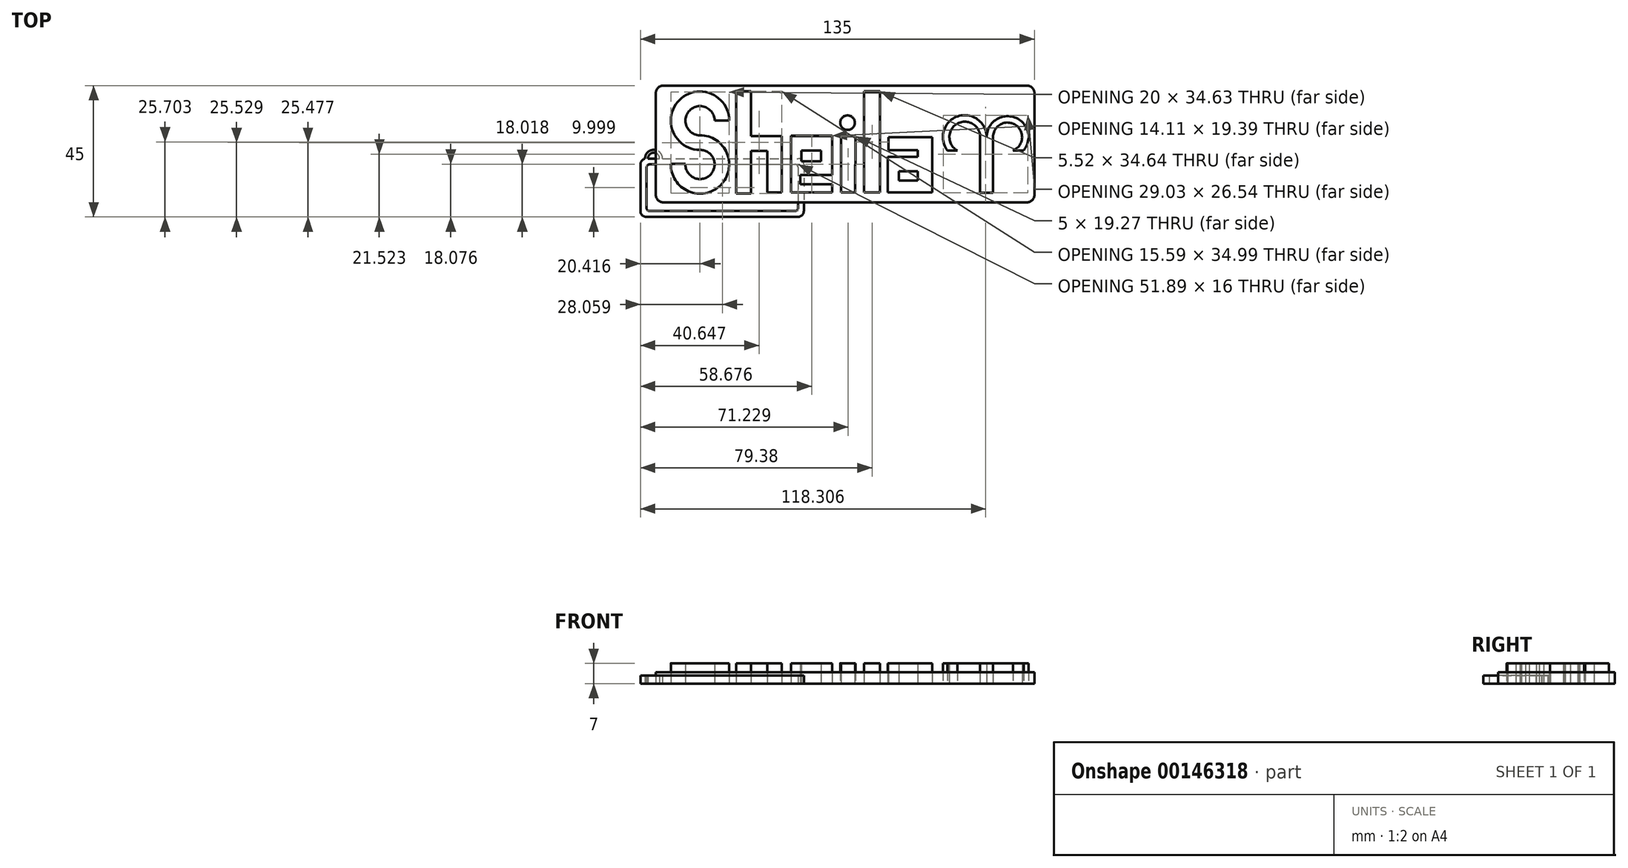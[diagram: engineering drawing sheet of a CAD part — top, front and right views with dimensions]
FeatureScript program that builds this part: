
annotation { "Feature Type Name" : "Feature", "Feature Type Description" : "" }
export const myFeature = defineFeature(function(context is Context, id is Id, definition is map)
    precondition{}
    {
        {
            var Q0;
            Q0=qCreatedBy(makeId("Top.planeOp"),FACE);
            var sketch = newSketch(context, id + "F0", { "sketchPlane" : qUnion([Q0])});
            skLineSegment(sketch, "E0.bottom", {"start": v(-68.38, 27.23) * mm, "end": v(61.38, 27.23) * mm});
            skLineSegment(sketch, "E0.top", {"start": v(-68.41, -22.77) * mm, "end": v(61.38, -22.77) * mm});
            skLineSegment(sketch, "E0.left", {"start": v(-73.62, 22) * mm, "end": v(-73.62, -17.56) * mm});
            skLineSegment(sketch, "E0.right", {"start": v(66.38, 22.23) * mm, "end": v(66.38, -17.77) * mm});
            skPoint(sketch, "E1.visualSharp", {"position": v(-73.62, 27.23) * mm});
            skArc(sketch, "E1.filletArc", {"start": v(-68.38, 27.23) * mm, "mid": v(-72.08, 25.7) * mm, "end": v(-73.62, 22) * mm});
            skPoint(sketch, "E2.visualSharp", {"position": v(-73.62, -22.77) * mm});
            skArc(sketch, "E2.filletArc", {"start": v(-73.62, -17.56) * mm, "mid": v(-72.1, -21.25) * mm, "end": v(-68.41, -22.77) * mm});
            skPoint(sketch, "E3.visualSharp", {"position": v(66.38, 27.23) * mm});
            skArc(sketch, "E3.filletArc", {"start": v(66.38, 22.23) * mm, "mid": v(64.92, 25.76) * mm, "end": v(61.38, 27.23) * mm});
            skPoint(sketch, "E4.visualSharp", {"position": v(66.38, -22.77) * mm});
            skArc(sketch, "E4.filletArc", {"start": v(61.38, -22.77) * mm, "mid": v(64.92, -21.3) * mm, "end": v(66.38, -17.77) * mm});
            skLineSegment(sketch, "E5", {"start": v(-58.07, -4.63) * mm, "end": v(-58.2, -4.63) * mm});
            skLineSegment(sketch, "E6", {"start": v(-40.77, 20.25) * mm, "end": v(-40.77, -14.74) * mm});
            skLineSegment(sketch, "E7.trimOffspring", {"start": v(-22, -14.39) * mm, "end": v(-7.9, -14.39) * mm});
            skLineSegment(sketch, "E8", {"start": v(-40.77, -14.74) * mm, "end": v(-35.77, -14.74) * mm});
            skLineSegment(sketch, "E9", {"start": v(-35.77, -14.74) * mm, "end": v(-35.77, -0.15) * mm});
            skLineSegment(sketch, "E10", {"start": v(-35.77, -0.15) * mm, "end": v(-30.2, -0.15) * mm});
            skLineSegment(sketch, "E11", {"start": v(-30.2, -0.15) * mm, "end": v(-30.2, -14.39) * mm});
            skLineSegment(sketch, "E12", {"start": v(-30.2, -14.39) * mm, "end": v(-25.18, -14.39) * mm});
            skLineSegment(sketch, "E13", {"start": v(-40.77, 20.25) * mm, "end": v(-35.77, 20.25) * mm});
            skLineSegment(sketch, "E14", {"start": v(-7.94, 5) * mm, "end": v(-22, 5) * mm});
            skLineSegment(sketch, "E15", {"start": v(-22, 5) * mm, "end": v(-22, -14.39) * mm});
            skLineSegment(sketch, "E16", {"start": v(-25.18, -14.39) * mm, "end": v(-25.18, 5.19) * mm});
            skLineSegment(sketch, "E17", {"start": v(-25.18, 4.88) * mm, "end": v(-35.77, 4.88) * mm});
            skLineSegment(sketch, "E18", {"start": v(-35.77, 4.88) * mm, "end": v(-35.77, 20.25) * mm});
            skLineSegment(sketch, "E19", {"start": v(-7.94, 5) * mm, "end": v(-7.94, -8.38) * mm});
            skLineSegment(sketch, "E20", {"start": v(-7.9, -14.39) * mm, "end": v(-7.9, -11.6) * mm});
            skLineSegment(sketch, "E21", {"start": v(-7.9, -11.6) * mm, "end": v(-18.85, -11.6) * mm});
            skLineSegment(sketch, "E22", {"start": v(-18.85, -11.6) * mm, "end": v(-18.85, -8.38) * mm});
            skLineSegment(sketch, "E23", {"start": v(-18.85, -8.38) * mm, "end": v(-7.94, -8.38) * mm});
            skLineSegment(sketch, "E24", {"start": v(-11.73, 0) * mm, "end": v(-11.73, -3.67) * mm});
            skLineSegment(sketch, "E25", {"start": v(-11.73, -3.67) * mm, "end": v(-18.48, -3.67) * mm});
            skLineSegment(sketch, "E26", {"start": v(-18.48, -3.67) * mm, "end": v(-18.48, 0) * mm});
            skLineSegment(sketch, "E27", {"start": v(-18.48, 0) * mm, "end": v(-11.73, 0) * mm});
            skLineSegment(sketch, "E28", {"start": v(-35.77, 4.88) * mm, "end": v(-25.18, 4.88) * mm});
            skLineSegment(sketch, "E29", {"start": v(-4.9, -14.39) * mm, "end": v(-4.9, 4.88) * mm});
            skLineSegment(sketch, "E30", {"start": v(-4.9, 4.88) * mm, "end": v(0.1, 4.87) * mm});
            skLineSegment(sketch, "E31", {"start": v(0.1, 4.87) * mm, "end": v(0, -14.39) * mm});
            skLineSegment(sketch, "E32", {"start": v(0, -14.39) * mm, "end": v(-4.9, -14.39) * mm});
            skLineSegment(sketch, "E33.trimOffspring", {"start": v(-4.9, -14.39) * mm, "end": v(0, -14.39) * mm});
            skCircle(sketch, "E34", {"center": v(-2.64, 9.53) * mm, "radius": 2.5 * mm});
            skLineSegment(sketch, "E35", {"start": v(3, 20.25) * mm, "end": v(3, -14.39) * mm});
            skLineSegment(sketch, "E36", {"start": v(3, -14.39) * mm, "end": v(8.52, -14.39) * mm});
            skLineSegment(sketch, "E37", {"start": v(8.52, -14.39) * mm, "end": v(8.52, 20.25) * mm});
            skLineSegment(sketch, "E38.trimOffspring", {"start": v(11.15, -14.39) * mm, "end": v(26.44, -14.39) * mm});
            skLineSegment(sketch, "E39", {"start": v(26.4, 4.6) * mm, "end": v(26.44, 4.6) * mm});
            skLineSegment(sketch, "E40", {"start": v(11.15, -14.39) * mm, "end": v(11.15, -2.12) * mm});
            skLineSegment(sketch, "E41", {"start": v(11.15, -2.12) * mm, "end": v(21.41, -2.12) * mm});
            skLineSegment(sketch, "E42", {"start": v(26.44, 4.6) * mm, "end": v(11.44, 4.6) * mm});
            skLineSegment(sketch, "E43", {"start": v(11.44, 4.6) * mm, "end": v(11.44, 0.12) * mm});
            skLineSegment(sketch, "E44", {"start": v(11.44, 0.12) * mm, "end": v(21.41, 0.12) * mm});
            skLineSegment(sketch, "E45", {"start": v(21.41, 0.12) * mm, "end": v(21.41, -2.2) * mm});
            skLineSegment(sketch, "E46", {"start": v(14.96, -7.12) * mm, "end": v(21.41, -7.12) * mm});
            skLineSegment(sketch, "E47", {"start": v(21.41, -7.12) * mm, "end": v(21.41, -10.27) * mm});
            skLineSegment(sketch, "E48", {"start": v(21.41, -10.27) * mm, "end": v(14.96, -10.27) * mm});
            skLineSegment(sketch, "E49", {"start": v(14.96, -10.27) * mm, "end": v(14.96, -7.12) * mm});
            skLineSegment(sketch, "E50", {"start": v(26.44, 4.6) * mm, "end": v(26.44, -14.39) * mm});
            skLineSegment(sketch, "E51", {"start": v(3, 20.25) * mm, "end": v(8.52, 20.25) * mm});
            skLineSegment(sketch, "E52.bottom", {"start": v(-65.84, 22.23) * mm, "end": v(58.88, 22.23) * mm});
            skLineSegment(sketch, "E52.top", {"start": v(-65.84, -17.77) * mm, "end": v(58.88, -17.77) * mm});
            skLineSegment(sketch, "E52.left", {"start": v(-68.34, 19.73) * mm, "end": v(-68.34, -15.27) * mm});
            skLineSegment(sketch, "E52.right", {"start": v(61.38, 19.73) * mm, "end": v(61.38, -15.27) * mm});
            skPoint(sketch, "E53.oppositeSnap0", {"position": v(-68.34, 2.23) * mm});
            skArc(sketch, "E54.filletArc", {"start": v(61.38, 19.73) * mm, "mid": v(60.65, 21.5) * mm, "end": v(58.88, 22.23) * mm});
            skArc(sketch, "E55.filletArc", {"start": v(58.88, -17.77) * mm, "mid": v(60.65, -17.04) * mm, "end": v(61.38, -15.27) * mm});
            skArc(sketch, "E56.filletArc", {"start": v(-65.84, 22.23) * mm, "mid": v(-67.6, 21.5) * mm, "end": v(-68.34, 19.73) * mm});
            skArc(sketch, "E57.filletArc", {"start": v(-68.34, -15.27) * mm, "mid": v(-67.6, -17.04) * mm, "end": v(-65.84, -17.77) * mm});
            skLineSegment(sketch, "E58.top", {"start": v(42.82, -14.52) * mm, "end": v(47.23, -14.52) * mm});
            skLineSegment(sketch, "E58.left", {"start": v(42.82, 4.6) * mm, "end": v(42.82, -14.52) * mm});
            skLineSegment(sketch, "E58.right", {"start": v(47.23, 4.6) * mm, "end": v(47.23, -14.52) * mm});
            skArc(sketch, "E59", {"start": v(45.04, 4.6) * mm, "mid": v(35.1, 11.7) * mm, "end": v(31.62, 0) * mm});
            skArc(sketch, "E60", {"start": v(42.82, 4.6) * mm, "mid": v(34.88, 9.16) * mm, "end": v(34.95, 0) * mm});
            skArc(sketch, "E61", {"start": v(54.09, 0) * mm, "mid": v(54.98, 8.73) * mm, "end": v(47.23, 4.6) * mm});
            skArc(sketch, "E62", {"start": v(57.7, 0) * mm, "mid": v(54.66, 11.34) * mm, "end": v(45.04, 4.6) * mm});
            skLineSegment(sketch, "E63", {"start": v(54.09, 0) * mm, "end": v(57.7, 0) * mm});
            skLineSegment(sketch, "E64", {"start": v(31.62, 0) * mm, "end": v(34.95, 0) * mm});
            skLineSegment(sketch, "E65.trimOffspring", {"start": v(-22, 4.88) * mm, "end": v(-7.94, 4.88) * mm});
            skArc(sketch, "E66", {"start": v(-54.68, 27.23) * mm, "mid": v(-62.26, 34.73) * mm, "end": v(-69.68, 27.07) * mm});
            skArc(sketch, "E67", {"start": v(-57.18, 27.23) * mm, "mid": v(-62.18, 32.23) * mm, "end": v(-67.18, 27.23) * mm});
            skLineSegment(sketch, "E68.bottom", {"start": v(-68.62, -22.77) * mm, "end": v(61.38, -22.77) * mm});
            skLineSegment(sketch, "E68.top", {"start": v(-68.62, 27.23) * mm, "end": v(61.38, 27.23) * mm});
            skLineSegment(sketch, "E68.left", {"start": v(-73.62, -17.77) * mm, "end": v(-73.62, 22.23) * mm});
            skLineSegment(sketch, "E68.right", {"start": v(66.38, -17.77) * mm, "end": v(66.38, 22.23) * mm});
            skArc(sketch, "E69.filletArc", {"start": v(-73.62, -17.77) * mm, "mid": v(-72.15, -21.3) * mm, "end": v(-68.62, -22.77) * mm});
            skArc(sketch, "E70.filletArc", {"start": v(-68.62, 27.23) * mm, "mid": v(-72.15, 25.76) * mm, "end": v(-73.62, 22.23) * mm});
            skArc(sketch, "E71", {"start": v(-43.2, 10.22) * mm, "mid": v(-60.28, 17.29) * mm, "end": v(-53.2, 0.22) * mm});
            skArc(sketch, "E72", {"start": v(-48.2, 10.22) * mm, "mid": v(-56.74, 13.75) * mm, "end": v(-53.2, 5.22) * mm});
            skArc(sketch, "E73", {"start": v(-58.2, -4.63) * mm, "mid": v(-49.72, -8.37) * mm, "end": v(-53.2, 0.22) * mm});
            skArc(sketch, "E74", {"start": v(-63.2, -4.63) * mm, "mid": v(-46.19, -11.9) * mm, "end": v(-53.2, 5.22) * mm});
            skLineSegment(sketch, "E75", {"start": v(-58.07, -4.63) * mm, "end": v(-63.2, -4.63) * mm});
            skLineSegment(sketch, "E76", {"start": v(-48.2, 10.22) * mm, "end": v(-43.2, 10.22) * mm});
            skSolve(sketch);
        }
        {
            var Q0;
            Q0 = qSketchRegion(id + "F0", true);
            extrude(context, id + "F1", {"entities" : qUnion([Q0]), "depth" : 7 * mm});
        }
        {
            var Q0;
            {var subQ4=sQuery(id+"F0.wireOp",EDGE,"8bLnSezT-o6uE-8m6s-4Zwt-f85QpU6h1ui9");Q0=makeQuery(id+"F0.imprint","IMPRINT",FACE,{"disambiguationData":[TD([[makeQuery(id+"F0.imprint","IMPRINT",EDGE,{"derivedFrom":subQ4}),-1.0]])]});}
            var Q1;
            Q1=makeQuery(id+"F0.imprint","IMPRINT",FACE,{"disambiguationData":[TD([[makeQuery(id+"F0.imprint","IMPRINT",EDGE,{"derivedFrom":sQuery(id+"F0.wireOp",EDGE,"E6")}),1.0]])]});
            var Q2;
            {var subQ2=sQuery(id+"F0.wireOp",EDGE,"E7.trimOffspring");Q2=makeQuery(id+"F0.imprint","IMPRINT",FACE,{"disambiguationData":[TD([[makeQuery(id+"F0.imprint","IMPRINT",EDGE,{"derivedFrom":subQ2}),1.0]])]});}
            var Q3;
            Q3=makeQuery(id+"F0.imprint","IMPRINT",FACE,{"disambiguationData":[TD([[makeQuery(id+"F0.imprint","IMPRINT",EDGE,{"derivedFrom":sQuery(id+"F0.wireOp",EDGE,"E29")}),-1.0]])]});
            var Q4;
            Q4=makeQuery(id+"F0.imprint","IMPRINT",FACE,{"disambiguationData":[TD([[makeQuery(id+"F0.imprint","IMPRINT",EDGE,{"derivedFrom":sQuery(id+"F0.wireOp",EDGE,"E34")}),1.0]])]});
            var Q5;
            Q5=makeQuery(id+"F0.imprint","IMPRINT",FACE,{"disambiguationData":[TD([[makeQuery(id+"F0.imprint","IMPRINT",EDGE,{"derivedFrom":sQuery(id+"F0.wireOp",EDGE,"E35")}),1.0]])]});
            var Q6;
            Q6=makeQuery(id+"F0.imprint","IMPRINT",FACE,{"disambiguationData":[TD([[makeQuery(id+"F0.imprint","IMPRINT",EDGE,{"derivedFrom":sQuery(id+"F0.wireOp",EDGE,"E38.trimOffspring")}),1.0]])]});
            var Q7;
            Q7=makeQuery(id+"F0.imprint","IMPRINT",FACE,{"disambiguationData":[TD([[makeQuery(id+"F0.imprint","IMPRINT",EDGE,{"derivedFrom":sQuery(id+"F0.wireOp",EDGE,"E58.top")}),1.0]])]});
            var Q8;
            Q8=makeQuery(id+"F0.imprint","IMPRINT",FACE,{"disambiguationData":[TD([[makeQuery(id+"F0.imprint","IMPRINT",EDGE,{"derivedFrom":sQuery(id+"F0.wireOp",EDGE,"E71")}),1.0]])]});
            extrude(context, id + "F2", {"entities" : qUnion([Q0, Q1, Q2, Q3, Q4, Q5, Q6, Q7, Q8]), "depth" : 7 * mm});
        }
        {
            var Q0;
            Q0=makeQuery(id+"F0.imprint","IMPRINT",FACE,{"disambiguationData":[TD([[makeQuery(id+"F0.imprint","IMPRINT",EDGE,{"derivedFrom":sQuery(id+"F0.wireOp",EDGE,"E6")}),-1.0]])]});
            var Q1;
            Q1=makeQuery(id+"F0.imprint","IMPRINT",FACE,{"disambiguationData":[TD([[makeQuery(id+"F0.imprint","IMPRINT",EDGE,{"derivedFrom":sQuery(id+"F0.wireOp",EDGE,"E46")}),-1.0]])]});
            var Q2;
            Q2=makeQuery(id+"F0.imprint","IMPRINT",FACE,{"disambiguationData":[TD([[makeQuery(id+"F0.imprint","IMPRINT",EDGE,{"derivedFrom":sQuery(id+"F0.wireOp",EDGE,"E24")}),-1.0]])]});
            extrude(context, id + "F3", {"entities" : qUnion([Q0, Q1, Q2]), "depth" : 4 * mm});
        }
        {
            var Q0;
            Q0=makeQuery(id+"F1.opExtrude","SWEPT_BODY",BODY,{"disambiguationData":[OSD([sQuery(id+"F0.wireOp",EDGE,"E52.bottom"),sQuery(id+"F0.wireOp",EDGE,"E52.top"),sQuery(id+"F0.wireOp",EDGE,"E52.left"),sQuery(id+"F0.wireOp",EDGE,"E52.right"),sQuery(id+"F0.wireOp",EDGE,"E54.filletArc"),sQuery(id+"F0.wireOp",EDGE,"E55.filletArc"),sQuery(id+"F0.wireOp",EDGE,"E56.filletArc"),sQuery(id+"F0.wireOp",EDGE,"E57.filletArc"),sQuery(id+"F0.wireOp",EDGE,"E66"),sQuery(id+"F0.wireOp",EDGE,"E67"),sQuery(id+"F0.wireOp",EDGE,"E68.bottom"),sQuery(id+"F0.wireOp",EDGE,"E68.top"),sQuery(id+"F0.wireOp",EDGE,"E68.left"),sQuery(id+"F0.wireOp",EDGE,"E68.right"),sQuery(id+"F0.wireOp",EDGE,"E69.filletArc"),sQuery(id+"F0.wireOp",EDGE,"E70.filletArc"),sQuery(id+"F0.wireOp",EDGE,"E3.filletArc"),sQuery(id+"F0.wireOp",EDGE,"E4.filletArc")])]});
            var Q1;
            Q1=sQuery(id+"F0.wireOp",VERTEX,"E2.visualSharp");
            transform(context, id + "F4", {"entities" : qUnion([Q0]), "transformType" : TransformType.SCALE_UNIFORMLY, "scale" : 0.4, "scalePoint" : qUnion([Q1]), "makeCopy" : false});
        }
    });
